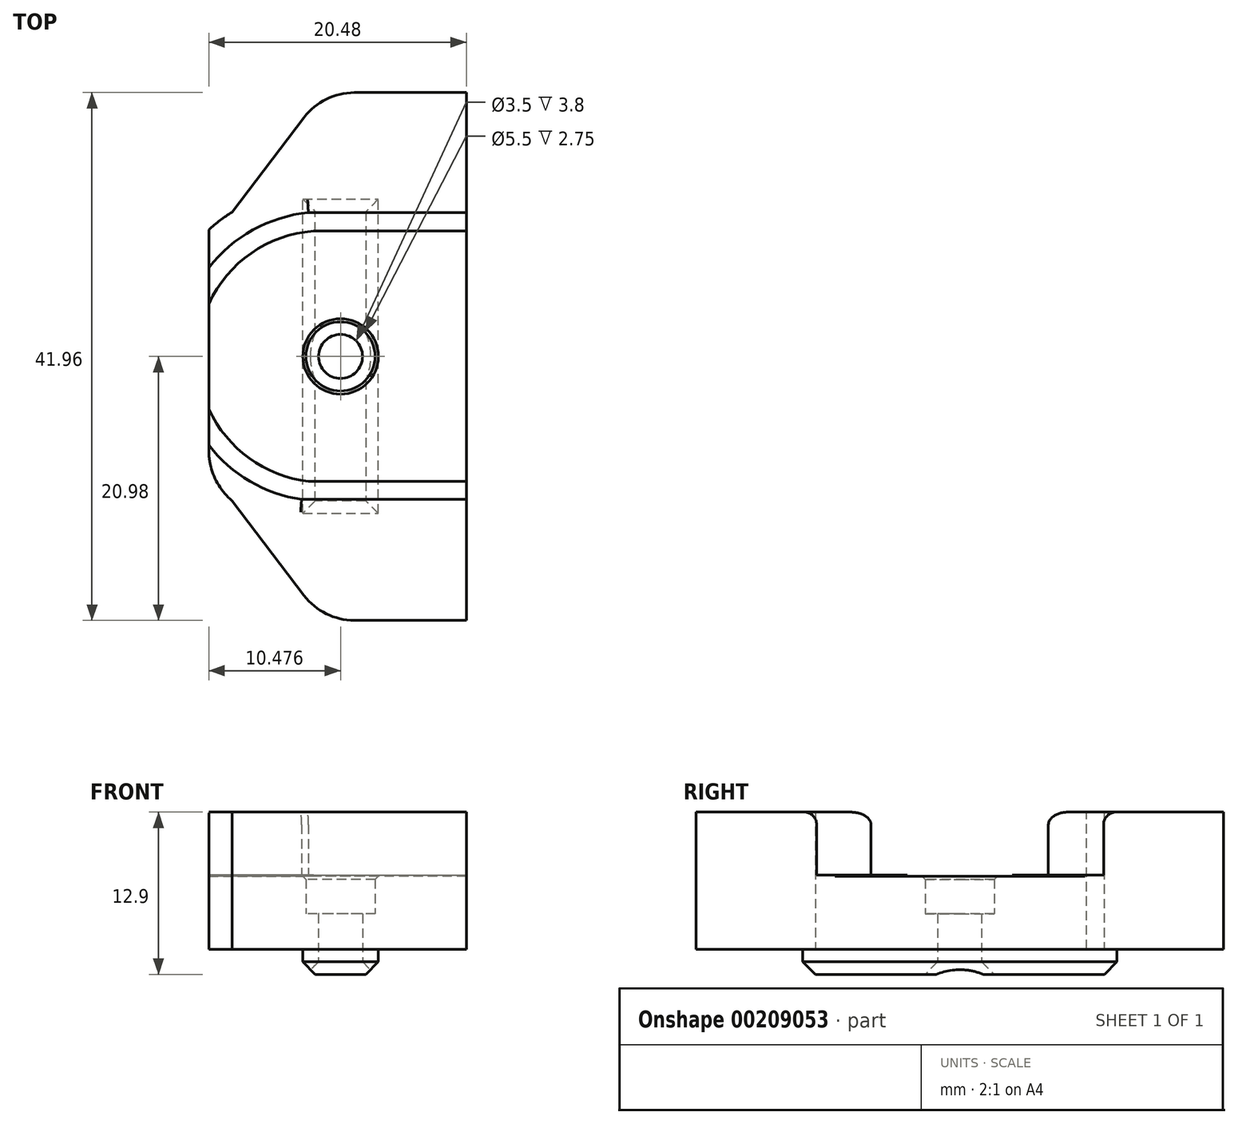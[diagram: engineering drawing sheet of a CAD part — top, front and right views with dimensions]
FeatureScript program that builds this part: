
annotation { "Feature Type Name" : "Feature", "Feature Type Description" : "" }
export const myFeature = defineFeature(function(context is Context, id is Id, definition is map)
    precondition{}
    {
        {
            assignVariable(context, id + "F0", {"name" : "Base_Thickness", "anyValue" : 4.2 - 1.4});
        }
        {
            assignVariable(context, id + "F1", {"name" : "Head_Height", "anyValue" : 3});
        }
        {
            assignVariable(context, id + "F2", {"name" : "Hub_Clearance", "anyValue" : 0.1});
        }
        {
            assignVariable(context, id + "F3", {"name" : "Bearing_Thickness", "anyValue" : 7});
        }
        {
            var Q0;
            Q0=qCreatedBy(makeId("Top.planeOp"),FACE);
            var sketch = newSketch(context, id + "F4", { "sketchPlane" : qUnion([Q0])});
            skCircle(sketch, "E0", {"center": v(0, 0) * mm, "radius": 10 * mm, "construction": true});
            skCircle(sketch, "E1", {"center": v(0, 0) * mm, "radius": 11.5 * mm, "construction": true});
            skArc(sketch, "E2", {"start": v(-0.76, 9.97) * mm, "mid": v(-10, 0.2) * mm, "end": v(-1.17, -9.93) * mm});
            skArc(sketch, "E3", {"start": v(-1.17, 11.44) * mm, "mid": v(-11.5, 0.27) * mm, "end": v(-1.7, -11.37) * mm});
            skLineSegment(sketch, "E4", {"start": v(-1.17, -9.93) * mm, "end": v(11.4, -9.93) * mm});
            skLineSegment(sketch, "E5", {"start": v(11.4, -9.93) * mm, "end": v(11.4, -11.37) * mm});
            skLineSegment(sketch, "E6", {"start": v(11.4, -11.37) * mm, "end": v(-1.7, -11.37) * mm});
            skLineSegment(sketch, "E7", {"start": v(-0.76, 9.97) * mm, "end": v(11.4, 9.97) * mm});
            skLineSegment(sketch, "E8", {"start": v(11.4, 9.97) * mm, "end": v(11.4, 11.44) * mm});
            skLineSegment(sketch, "E9", {"start": v(11.4, 11.44) * mm, "end": v(-1.17, 11.44) * mm});
            skLineSegment(sketch, "E10", {"start": v(11.4, 9.97) * mm, "end": v(11.4, -9.93) * mm});
            skArc(sketch, "E11", {"start": v(-1.2, 13.51) * mm, "mid": v(-13.56, 0.17) * mm, "end": v(-1.53, -13.48) * mm});
            skLineSegment(sketch, "E12", {"start": v(-1.2, 13.51) * mm, "end": v(11.4, 13.51) * mm});
            skLineSegment(sketch, "E13", {"start": v(11.4, 13.51) * mm, "end": v(11.4, 11.44) * mm});
            skLineSegment(sketch, "E14", {"start": v(-1.53, -13.48) * mm, "end": v(11.4, -13.48) * mm});
            skLineSegment(sketch, "E15", {"start": v(11.4, -13.48) * mm, "end": v(11.4, -11.37) * mm});
            skCircle(sketch, "E16", {"center": v(1.4, 0) * mm, "radius": 1.75 * mm});
            skCircle(sketch, "E17", {"center": v(1.4, 0) * mm, "radius": 2.75 * mm});
            skSolve(sketch);
        }
        {
            var Q0;
            Q0=makeQuery(id+"F4.imprint","IMPRINT",FACE,{"disambiguationData":[TD([[makeQuery(id+"F4.imprint","IMPRINT",EDGE,{"derivedFrom":sQuery(id+"F4.wireOp",EDGE,"E3")}),-1.0]])]});
            var Q1;
            Q1=makeQuery(id+"F4.imprint","IMPRINT",FACE,{"disambiguationData":[TD([[makeQuery(id+"F4.imprint","IMPRINT",EDGE,{"derivedFrom":sQuery(id+"F4.wireOp",EDGE,"E2")}),-1.0]])]});
            var Q2;
            Q2=makeQuery(id+"F4.imprint","IMPRINT",FACE,{"disambiguationData":[TD([[makeQuery(id+"F4.imprint","IMPRINT",EDGE,{"derivedFrom":sQuery(id+"F4.wireOp",EDGE,"E16")}),-1.0]])]});
            var Q3;
            Q3=makeQuery(id+"F4.imprint","IMPRINT",FACE,{"disambiguationData":[TD([[makeQuery(id+"F4.imprint","IMPRINT",EDGE,{"derivedFrom":sQuery(id+"F4.wireOp",EDGE,"E2")}),1.0]])]});
            extrude(context, id + "F5", {"entities" : qUnion([Q0, Q1, Q2, Q3]), "depth" : (getVariable(context, 'Base_Thickness')) * mm});
        }
        {
            var Q0;
            Q0=makeQuery(id+"F4.imprint","IMPRINT",FACE,{"disambiguationData":[TD([[makeQuery(id+"F4.imprint","IMPRINT",EDGE,{"derivedFrom":sQuery(id+"F4.wireOp",EDGE,"E2")}),1.0]])]});
            var Q1;
            Q1=makeQuery(id+"F4.imprint","IMPRINT",FACE,{"disambiguationData":[TD([[makeQuery(id+"F4.imprint","IMPRINT",EDGE,{"derivedFrom":sQuery(id+"F4.wireOp",EDGE,"E2")}),-1.0]])]});
            var Q2;
            Q2=makeQuery(id+"F4.imprint","IMPRINT",FACE,{"disambiguationData":[TD([[makeQuery(id+"F4.imprint","IMPRINT",EDGE,{"derivedFrom":sQuery(id+"F4.wireOp",EDGE,"E3")}),-1.0]])]});
            extrude(context, id + "F6", {"entities" : qUnion([Q0, Q1, Q2]), "operationType" : NewBodyOperationType.ADD, "depth" : (getVariable(context, 'Base_Thickness') + getVariable(context, 'Head_Height')) * mm});
        }
        {
            var Q0;
            Q0=makeQuery(id+"F4.imprint","IMPRINT",FACE,{"disambiguationData":[TD([[makeQuery(id+"F4.imprint","IMPRINT",EDGE,{"derivedFrom":sQuery(id+"F4.wireOp",EDGE,"E2")}),-1.0]])]});
            var Q1;
            Q1=makeQuery(id+"F4.imprint","IMPRINT",FACE,{"disambiguationData":[TD([[makeQuery(id+"F4.imprint","IMPRINT",EDGE,{"derivedFrom":sQuery(id+"F4.wireOp",EDGE,"E3")}),-1.0]])]});
            extrude(context, id + "F7", {"entities" : qUnion([Q0, Q1]), "operationType" : NewBodyOperationType.ADD, "depth" : (getVariable(context, 'Base_Thickness') + getVariable(context, 'Head_Height') + getVariable(context, 'Hub_Clearance')) * mm});
        }
        {
            var Q0;
            Q0=makeQuery(id+"F4.imprint","IMPRINT",FACE,{"disambiguationData":[TD([[makeQuery(id+"F4.imprint","IMPRINT",EDGE,{"derivedFrom":sQuery(id+"F4.wireOp",EDGE,"E3")}),-1.0]])]});
            extrude(context, id + "F8", {"entities" : qUnion([Q0]), "operationType" : NewBodyOperationType.ADD, "depth" : (getVariable(context, 'Base_Thickness') + getVariable(context, 'Head_Height') + getVariable(context, 'Hub_Clearance') + getVariable(context, 'Bearing_Thickness') - 2) * mm});
        }
        {
            var Q0;
            Q0=makeQuery(id+"F5.opExtrude","CAP_FACE",FACE,{"disambiguationData":[OSD([sQuery(id+"F4.wireOp",EDGE,"E5"),sQuery(id+"F4.wireOp",EDGE,"E8"),sQuery(id+"F4.wireOp",EDGE,"E10"),sQuery(id+"F4.wireOp",EDGE,"E11"),sQuery(id+"F4.wireOp",EDGE,"E12"),sQuery(id+"F4.wireOp",EDGE,"E13"),sQuery(id+"F4.wireOp",EDGE,"E14"),sQuery(id+"F4.wireOp",EDGE,"E15"),sQuery(id+"F4.wireOp",EDGE,"E16")])],"isStart":true});
            var sketch = newSketch(context, id + "F9", { "sketchPlane" : qUnion([Q0])});
            skLineSegment(sketch, "E18", {"start": v(1.4, -12.51) * mm, "end": v(1.4, 12.48) * mm, "construction": true});
            skLineSegment(sketch, "E19.bottom", {"start": v(-1.6, 12.48) * mm, "end": v(4.4, 12.48) * mm});
            skLineSegment(sketch, "E19.top", {"start": v(-1.6, -12.51) * mm, "end": v(4.4, -12.51) * mm});
            skLineSegment(sketch, "E19.left", {"start": v(-1.6, 12.48) * mm, "end": v(-1.6, -12.51) * mm});
            skLineSegment(sketch, "E19.right", {"start": v(4.4, 12.48) * mm, "end": v(4.4, -12.51) * mm});
            skSolve(sketch);
        }
        {
            var Q0;
            {var subQ4=sQuery(id+"F9.wireOp",EDGE,"E19.bottom");Q0=makeQuery(id+"F9.imprint","IMPRINT",FACE,{"disambiguationData":[TD([[makeQuery(id+"F9.imprint","IMPRINT",EDGE,{"derivedFrom":subQ4}),-1.0]])]});}
            var Q1;
            {var subQ0=sQuery(id+"F9.wireOp",EDGE,"E19.top");Q1=makeQuery(id+"F9.imprint","IMPRINT",FACE,{"disambiguationData":[TD([[makeQuery(id+"F9.imprint","IMPRINT",EDGE,{"derivedFrom":subQ0}),1.0]])]});}
            extrude(context, id + "F10", {"entities" : qUnion([Q0, Q1]), "operationType" : NewBodyOperationType.ADD, "depth" : 2 * mm});
        }
        {
            var Q0;
            {var subQ0=sQuery(id+"F4.wireOp",EDGE,"E14");Q0=makeQuery(id+"F8.boolean.opBoolean","MERGE",FACE,{"derivedFrom":[makeQuery(id+"F7.boolean.opBoolean","MERGE",FACE,{"derivedFrom":[makeQuery(id+"F6.boolean.opBoolean","MERGE",FACE,{"derivedFrom":[makeQuery(id+"F5.opExtrude","SWEPT_FACE",FACE,{"disambiguationData":[OSD([subQ0])]}),makeQuery(id+"F6.opExtrude","SWEPT_FACE",FACE,{"disambiguationData":[OSD([subQ0])]})]}),makeQuery(id+"F7.opExtrude","SWEPT_FACE",FACE,{"disambiguationData":[OSD([subQ0])]})]}),makeQuery(id+"F8.opExtrude","SWEPT_FACE",FACE,{"disambiguationData":[OSD([subQ0])]})]});}
            var sketch = newSketch(context, id + "F11", { "sketchPlane" : qUnion([Q0])});
            skLineSegment(sketch, "E20", {"start": v(-1.53, 10.9) * mm, "end": v(11.4, 10.9) * mm});
            skLineSegment(sketch, "E21", {"start": v(-1.53, 10.9) * mm, "end": v(11.4, 4.8) * mm});
            skLineSegment(sketch, "E22", {"start": v(11.4, 4.8) * mm, "end": v(11.4, 10.9) * mm});
            skSolve(sketch);
        }
        {
            var Q0;
            Q0=makeQuery(id+"F10.opExtrude","CAP_EDGE",EDGE,{"disambiguationData":[OSD([sQuery(id+"F9.wireOp",EDGE,"E19.right")])],"isStart":false});
            var Q1;
            Q1=makeQuery(id+"F10.opExtrude","CAP_EDGE",EDGE,{"disambiguationData":[OSD([sQuery(id+"F9.wireOp",EDGE,"E19.left")])],"isStart":false});
            var Q2;
            Q2=makeQuery(id+"F10.opExtrude","CAP_EDGE",EDGE,{"disambiguationData":[OSD([sQuery(id+"F9.wireOp",EDGE,"E19.bottom")])],"isStart":false});
            var Q3;
            Q3=makeQuery(id+"F10.opExtrude","CAP_EDGE",EDGE,{"disambiguationData":[OSD([sQuery(id+"F9.wireOp",EDGE,"E19.top")])],"isStart":false});
            var Q4;
            Q4=makeQuery(id+"F10.opExtrude","CAP_EDGE",EDGE,{"disambiguationData":[OSD([sQuery(id+"F4.wireOp",EDGE,"E16")])],"isStart":false});
            chamfer(context, id + "F12", {"entities" : qUnion([Q0, Q1, Q2, Q3, Q4]), "width" : 1 * mm, "tangentPropagation" : true});
        }
        {
            var Q0;
            Q0=makeQuery(id+"F6.opExtrude","CAP_EDGE",EDGE,{"disambiguationData":[OSD([sQuery(id+"F4.wireOp",EDGE,"E17")])],"isStart":false});
            chamfer(context, id + "F13", {"entities" : qUnion([Q0]), "width" : .25 * mm, "tangentPropagation" : true});
        }
        {
            var Q0;
            Q0=makeQuery(id+"F5.opExtrude","CAP_FACE",FACE,{"disambiguationData":[OSD([sQuery(id+"F4.wireOp",EDGE,"E5"),sQuery(id+"F4.wireOp",EDGE,"E8"),sQuery(id+"F4.wireOp",EDGE,"E10"),sQuery(id+"F4.wireOp",EDGE,"E11"),sQuery(id+"F4.wireOp",EDGE,"E12"),sQuery(id+"F4.wireOp",EDGE,"E13"),sQuery(id+"F4.wireOp",EDGE,"E14"),sQuery(id+"F4.wireOp",EDGE,"E15"),sQuery(id+"F4.wireOp",EDGE,"E16")])],"isStart":true});
            var sketch = newSketch(context, id + "F14", { "sketchPlane" : qUnion([Q0])});
            skLineSegment(sketch, "E23", {"start": v(11.4, 20.98) * mm, "end": v(0, 20.98) * mm});
            skLineSegment(sketch, "E24", {"start": v(0, 20.98) * mm, "end": v(-7.23, 11.48) * mm});
            skLineSegment(sketch, "E25", {"start": v(-7.23, 11.48) * mm, "end": v(11.4, 11.48) * mm});
            skLineSegment(sketch, "E26", {"start": v(11.4, 11.48) * mm, "end": v(11.4, 20.98) * mm});
            skLineSegment(sketch, "E27.MirrorCS", {"start": v(11.4, -20.98) * mm, "end": v(0, -20.98) * mm});
            skLineSegment(sketch, "E28.MirrorCS", {"start": v(0, -20.98) * mm, "end": v(-7.23, -11.48) * mm});
            skLineSegment(sketch, "E29.MirrorCS", {"start": v(-7.23, -11.48) * mm, "end": v(11.4, -11.48) * mm});
            skLineSegment(sketch, "E30.MirrorCS", {"start": v(11.4, -11.48) * mm, "end": v(11.4, -20.98) * mm});
            skSolve(sketch);
        }
        {
            var Q0;
            {var subQ2=sQuery(id+"F14.wireOp",EDGE,"E23");Q0=makeQuery(id+"F14.imprint","IMPRINT",FACE,{"disambiguationData":[TD([[makeQuery(id+"F14.imprint","IMPRINT",EDGE,{"derivedFrom":subQ2}),1.0]])]});}
            var Q1;
            {var subQ2=sQuery(id+"F14.wireOp",EDGE,"E27.MirrorCS");Q1=makeQuery(id+"F14.imprint","IMPRINT",FACE,{"disambiguationData":[TD([[makeQuery(id+"F14.imprint","IMPRINT",EDGE,{"derivedFrom":subQ2}),-1.0]])]});}
            extrude(context, id + "F15", {"entities" : qUnion([Q0, Q1]), "operationType" : NewBodyOperationType.ADD, "oppositeDirection" : true, "depth" : 10.9 * mm});
        }
        {
            var Q0;
            {var subQ0=sQuery(id+"F4.wireOp",EDGE,"E12");var subQ1=sQuery(id+"F4.wireOp",EDGE,"E11");var subQ2=sQuery(id+"F4.wireOp",EDGE,"E14");Q0=makeQuery(id+"F15.boolean.opBoolean","MERGE",FACE,{"derivedFrom":[makeQuery(id+"F8.opExtrude","CAP_FACE",FACE,{"disambiguationData":[OSD([sQuery(id+"F4.wireOp",EDGE,"E3"),sQuery(id+"F4.wireOp",EDGE,"E6"),sQuery(id+"F4.wireOp",EDGE,"E9"),subQ1,subQ0,sQuery(id+"F4.wireOp",EDGE,"E13"),subQ2,sQuery(id+"F4.wireOp",EDGE,"E15")])],"isStart":false}),makeQuery(id+"F15.opExtrude","CAP_FACE",FACE,{"disambiguationData":[OSD([subQ1,subQ2,sQuery(id+"F14.wireOp",EDGE,"E23"),sQuery(id+"F14.wireOp",EDGE,"E24"),sQuery(id+"F14.wireOp",EDGE,"E26")])],"isStart":false}),makeQuery(id+"F15.opExtrude","CAP_FACE",FACE,{"disambiguationData":[OSD([subQ1,subQ0,sQuery(id+"F14.wireOp",EDGE,"E27.MirrorCS"),sQuery(id+"F14.wireOp",EDGE,"E28.MirrorCS"),sQuery(id+"F14.wireOp",EDGE,"E30.MirrorCS")])],"isStart":false})]});}
            var sketch = newSketch(context, id + "F16", { "sketchPlane" : qUnion([Q0])});
            skLineSegment(sketch, "E31.bottom", {"start": v(-9.08, 10.08) * mm, "end": v(-13.57, 10.08) * mm});
            skLineSegment(sketch, "E31.top", {"start": v(-9.08, -10.08) * mm, "end": v(-13.57, -10.08) * mm});
            skLineSegment(sketch, "E31.left", {"start": v(-9.08, 10.08) * mm, "end": v(-9.08, -10.08) * mm});
            skLineSegment(sketch, "E31.right", {"start": v(-13.57, 10.08) * mm, "end": v(-13.57, -10.08) * mm});
            skSolve(sketch);
        }
        {
            var Q0;
            {var subQ0=sQuery(id+"F16.wireOp",EDGE,"E31.left");var subQ1=makeQuery(id+"F8.opExtrude","CAP_EDGE",EDGE,{"disambiguationData":[OSD([sQuery(id+"F4.wireOp",EDGE,"E3")])],"isStart":false});var subQ2=makeQuery(id+"F16.imprint","INTERSECT",VERTEX,{"disambiguationData":[OD(0.0)],"derivedFrom":[subQ1,subQ0]});Q0=makeQuery(id+"F16.imprint","IMPRINT",FACE,{"disambiguationData":[TD([[makeQuery(id+"F16.imprint","IMPRINT",EDGE,{"disambiguationData":[TD([[subQ2,-1.0]])],"derivedFrom":subQ1}),-1.0]])]});}
            var Q1;
            {var subQ0=sQuery(id+"F16.wireOp",EDGE,"E31.left");var subQ1=makeQuery(id+"F8.opExtrude","CAP_EDGE",EDGE,{"disambiguationData":[OSD([sQuery(id+"F4.wireOp",EDGE,"E3")])],"isStart":false});var subQ2=makeQuery(id+"F16.imprint","INTERSECT",VERTEX,{"disambiguationData":[OD(0.0)],"derivedFrom":[subQ1,subQ0]});Q1=makeQuery(id+"F16.imprint","IMPRINT",FACE,{"disambiguationData":[TD([[makeQuery(id+"F16.imprint","IMPRINT",EDGE,{"disambiguationData":[TD([[subQ2,-1.0]])],"derivedFrom":subQ0}),-1.0]])]});}
            extrude(context, id + "F17", {"entities" : qUnion([Q0, Q1]), "operationType" : NewBodyOperationType.REMOVE, "endBound" : BoundingType.THROUGH_ALL, "oppositeDirection" : true, "depth" : 25 * mm});
        }
        {
            var Q0;
            Q0=makeQuery(id+"F17.boolean.opBoolean","COPY",EDGE,{"derivedFrom":makeQuery(id+"F17.opExtrude","SWEPT_EDGE",EDGE,{"disambiguationData":[OSD([sQuery(id+"F4.wireOp",EDGE,"E11"),sQuery(id+"F16.wireOp",EDGE,"E31.bottom"),sQuery(id+"F16.wireOp",EDGE,"E31.left")])]})});
            var Q1;
            Q1=makeQuery(id+"F17.boolean.opBoolean","COPY",EDGE,{"derivedFrom":makeQuery(id+"F17.opExtrude","SWEPT_EDGE",EDGE,{"disambiguationData":[OSD([sQuery(id+"F4.wireOp",EDGE,"E11"),sQuery(id+"F16.wireOp",EDGE,"E31.top"),sQuery(id+"F16.wireOp",EDGE,"E31.left")])]})});
            fillet(context, id + "F18", {"entities" : qUnion([Q0, Q1]), "radius" : 5.3 * mm, "tangentPropagation" : true, "allowEdgeOverflow" : false});
        }
        {
            var Q0;
            Q0=makeQuery(id+"F15.opExtrude","SWEPT_EDGE",EDGE,{"disambiguationData":[OSD([sQuery(id+"F14.wireOp",EDGE,"E23"),sQuery(id+"F14.wireOp",EDGE,"E24")])]});
            var Q1;
            Q1=makeQuery(id+"F15.opExtrude","SWEPT_EDGE",EDGE,{"disambiguationData":[OSD([sQuery(id+"F14.wireOp",EDGE,"E27.MirrorCS"),sQuery(id+"F14.wireOp",EDGE,"E28.MirrorCS")])]});
            fillet(context, id + "F19", {"entities" : qUnion([Q0, Q1]), "radius" : 5 * mm, "tangentPropagation" : true, "allowEdgeOverflow" : false});
        }
        {
            var Q0;
            {var subQ3=sQuery(id+"F4.wireOp",EDGE,"E6");var subQ4=sQuery(id+"F4.wireOp",EDGE,"E3");Q0=makeQuery(id+"F17.boolean.opBoolean","SPLIT",EDGE,{"disambiguationData":[TD([makeQuery(id+"F8.opExtrude","SWEPT_FACE",FACE,{"disambiguationData":[OSD([subQ3])]})])],"derivedFrom":makeQuery(id+"F8.opExtrude","CAP_EDGE",EDGE,{"disambiguationData":[OSD([subQ4])],"isStart":false})});}
            var Q1;
            Q1=makeQuery(id+"F8.opExtrude","CAP_EDGE",EDGE,{"disambiguationData":[OSD([sQuery(id+"F4.wireOp",EDGE,"E6")])],"isStart":false});
            var Q2;
            {var subQ2=sQuery(id+"F4.wireOp",EDGE,"E9");var subQ4=sQuery(id+"F4.wireOp",EDGE,"E3");Q2=makeQuery(id+"F17.boolean.opBoolean","SPLIT",EDGE,{"disambiguationData":[TD([makeQuery(id+"F8.opExtrude","SWEPT_FACE",FACE,{"disambiguationData":[OSD([subQ2])]})])],"derivedFrom":makeQuery(id+"F8.opExtrude","CAP_EDGE",EDGE,{"disambiguationData":[OSD([subQ4])],"isStart":false})});}
            var Q3;
            Q3=makeQuery(id+"F8.opExtrude","CAP_EDGE",EDGE,{"disambiguationData":[OSD([sQuery(id+"F4.wireOp",EDGE,"E9")])],"isStart":false});
            fillet(context, id + "F20", {"entities" : qUnion([Q0, Q1, Q2, Q3]), "radius" : 1 * mm, "tangentPropagation" : true, "allowEdgeOverflow" : false});
        }
    });
